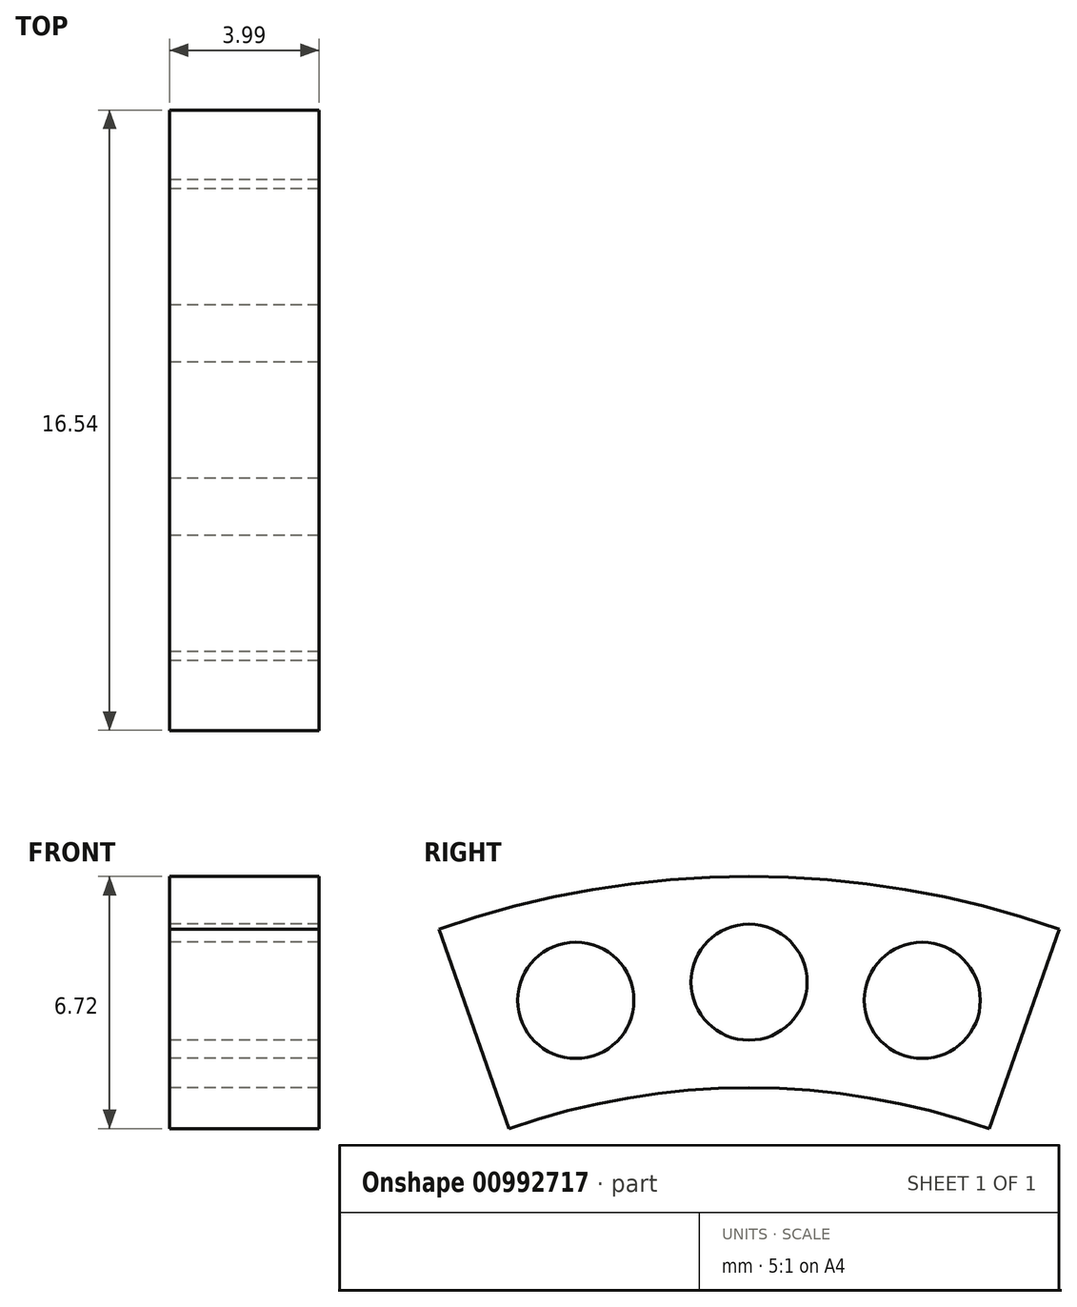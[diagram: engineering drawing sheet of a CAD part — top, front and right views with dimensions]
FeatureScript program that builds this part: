
annotation { "Feature Type Name" : "Feature", "Feature Type Description" : "" }
export const myFeature = defineFeature(function(context is Context, id is Id, definition is map)
    precondition{}
    {
        {
            var Q0;
            Q0=qCreatedBy(makeId("Right.planeOp"),FACE);
            var sketch = newSketch(context, id + "F0", { "sketchPlane" : qUnion([Q0])});
            skCircle(sketch, "E0", {"center": v(0, 0) * mm, "radius": 23.42 * mm, "construction": true});
            skLineSegment(sketch, "E1", {"start": v(0, 0) * mm, "end": v(-4.87, 22.9) * mm, "construction": true});
            skLineSegment(sketch, "E2", {"start": v(0, 0) * mm, "end": v(4.87, 22.9) * mm, "construction": true});
            skCircle(sketch, "E3", {"center": v(0, 0) * mm, "radius": 21.03 * mm, "construction": true});
            skCircle(sketch, "E4", {"center": v(0, 0) * mm, "radius": 22.23 * mm, "construction": true});
            skCircle(sketch, "E5", {"center": v(4.62, 21.74) * mm, "radius": 1.2 * mm, "construction": true});
            skCircle(sketch, "E6", {"center": v(-4.62, 21.74) * mm, "radius": 1.2 * mm, "construction": true});
            skCircle(sketch, "E7", {"center": v(0, 22.23) * mm, "radius": 1.2 * mm, "construction": true});
            skCircle(sketch, "E8", {"center": v(4.62, 21.74) * mm, "radius": 1.98 * mm, "construction": true});
            skCircle(sketch, "E9", {"center": v(0, 22.23) * mm, "radius": 1.98 * mm, "construction": true});
            skCircle(sketch, "E10", {"center": v(-4.62, 21.74) * mm, "radius": 1.98 * mm, "construction": true});
            skSolve(sketch);
        }
        {
            var Q0;
            Q0=qCreatedBy(makeId("Right.planeOp"),FACE);
            var sketch = newSketch(context, id + "F1", { "sketchPlane" : qUnion([Q0])});
            skCircle(sketch, "E11", {"center": v(4.62, 21.74) * mm, "radius": 1.55 * mm});
            skCircle(sketch, "E12", {"center": v(0, 22.23) * mm, "radius": 1.55 * mm});
            skCircle(sketch, "E13", {"center": v(-4.62, 21.74) * mm, "radius": 1.55 * mm});
            skLineSegment(sketch, "E14", {"start": v(0, 0) * mm, "end": v(-7.73, 22.1) * mm, "construction": true});
            skLineSegment(sketch, "E15", {"start": v(0, 0) * mm, "end": v(7.73, 22.1) * mm, "construction": true});
            skArc(sketch, "E16", {"start": v(-8.27, 23.64) * mm, "mid": v(0, 25.04) * mm, "end": v(8.27, 23.64) * mm});
            skArc(sketch, "E17", {"start": v(-6.4, 18.32) * mm, "mid": v(0, 19.4) * mm, "end": v(6.4, 18.32) * mm});
            skLineSegment(sketch, "E18", {"start": v(-8.27, 23.64) * mm, "end": v(-6.4, 18.32) * mm});
            skLineSegment(sketch, "E19", {"start": v(8.27, 23.64) * mm, "end": v(6.4, 18.32) * mm});
            skSolve(sketch);
        }
        {
            var Q0;
            Q0=qSketchRegion(id+"F1",true);
            extrude(context, id + "F2", {"entities" : qUnion([Q0]), "depth" : 4 * mm, "offsetDistance" : 25.4 * mm});
        }
    });
